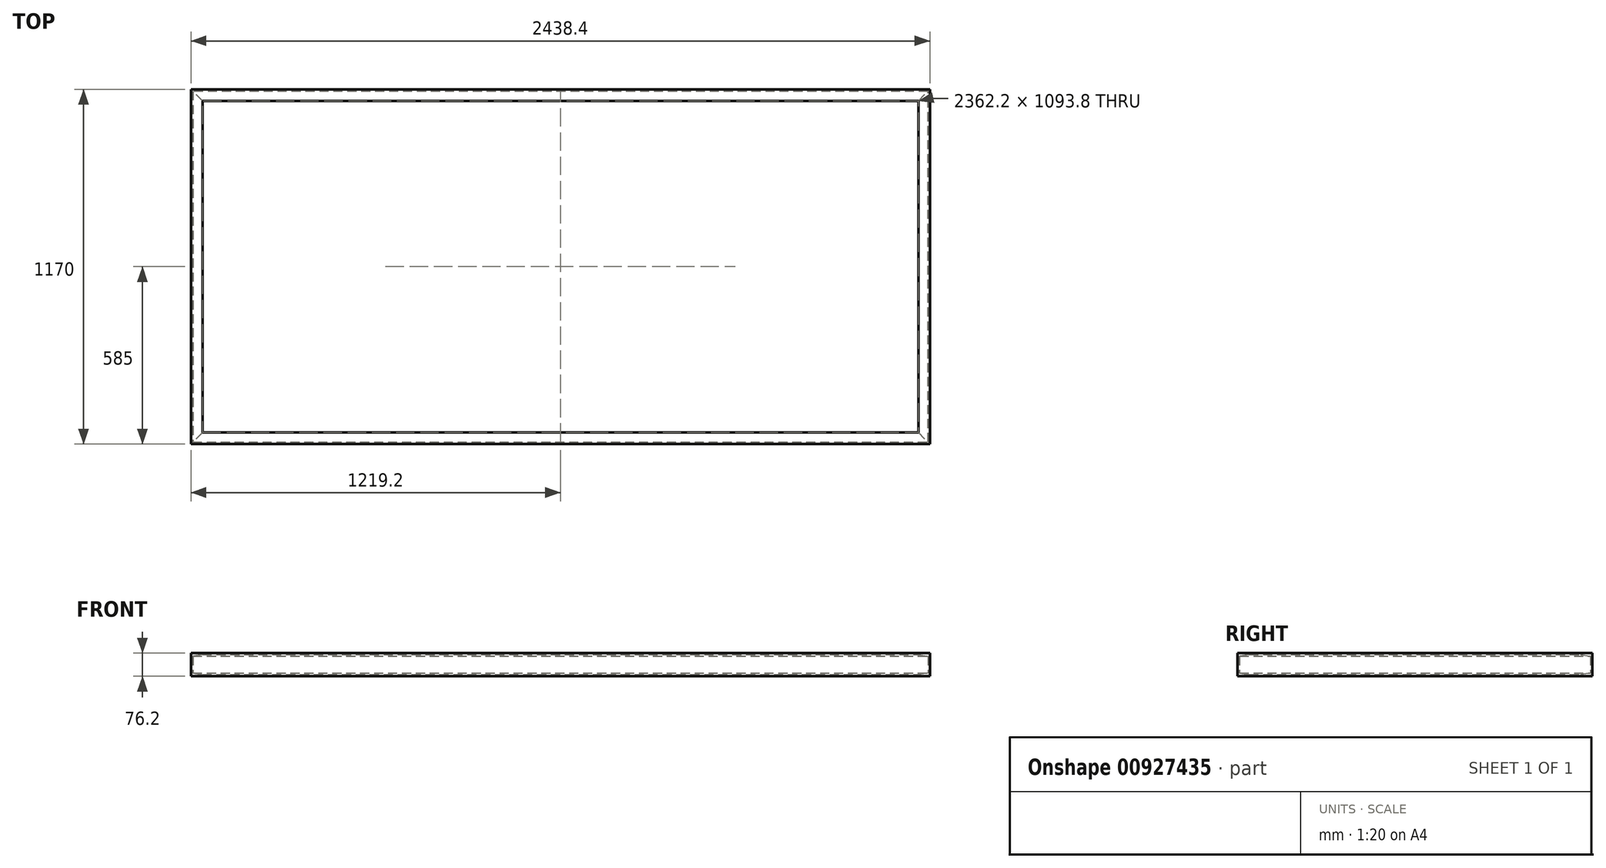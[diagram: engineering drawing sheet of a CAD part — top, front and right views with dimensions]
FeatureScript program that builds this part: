
annotation { "Feature Type Name" : "Feature", "Feature Type Description" : "" }
export const myFeature = defineFeature(function(context is Context, id is Id, definition is map)
    precondition{}
    {
        {
            var Q0;
            Q0=qCreatedBy(makeId("Top.planeOp"),FACE);
            var sketch = newSketch(context, id + "F0", { "sketchPlane" : qUnion([Q0])});
            skLineSegment(sketch, "E0.bottom", {"start": v(0, 0) * mm, "end": v(2438.4, 0) * mm});
            skLineSegment(sketch, "E0.top", {"start": v(0, 1170) * mm, "end": v(2438.4, 1170) * mm});
            skLineSegment(sketch, "E0.left", {"start": v(0, 0) * mm, "end": v(0, 1170) * mm});
            skLineSegment(sketch, "E0.right", {"start": v(2438.4, 0) * mm, "end": v(2438.4, 1170) * mm});
            skSolve(sketch);
        }
        {
            var Q0;
            Q0=qCreatedBy(makeId("Right.planeOp"),FACE);
            var sketch = newSketch(context, id + "F1", { "sketchPlane" : qUnion([Q0])});
            skLineSegment(sketch, "E1", {"start": v(0, 0) * mm, "end": v(0, -76.2) * mm});
            skLineSegment(sketch, "E2.MirrorCS", {"start": v(38.1, -5.08) * mm, "end": v(38.1, 0) * mm});
            skLineSegment(sketch, "E3.MirrorCS", {"start": v(38.1, -76.2) * mm, "end": v(38.1, -71.12) * mm});
            skLineSegment(sketch, "E4.MirrorCS", {"start": v(6.35, -10) * mm, "end": v(38.1, -5.08) * mm});
            skLineSegment(sketch, "E5.MirrorCS", {"start": v(0, -76.2) * mm, "end": v(38.1, -76.2) * mm});
            skLineSegment(sketch, "E6.MirrorCS", {"start": v(6.35, -66.2) * mm, "end": v(6.35, -10) * mm});
            skLineSegment(sketch, "E7.MirrorCS", {"start": v(38.1, -71.12) * mm, "end": v(6.35, -66.2) * mm});
            skLineSegment(sketch, "E8.MirrorCS", {"start": v(38.1, 0) * mm, "end": v(0, 0) * mm});
            skSolve(sketch);
        }
        {
            var Q0;
            Q0 = qSketchRegion(id + "F1", true);
            var Q1;
            Q1 = qConstructionFilter(qBodyType(qCreatedBy(id + "F0" ,EDGE), BodyType.WIRE), ConstructionObject.NO);
            sweep(context, id + "F2", {"profiles" : qUnion([Q0]), "path" : qUnion([Q1])});
        }
    });
